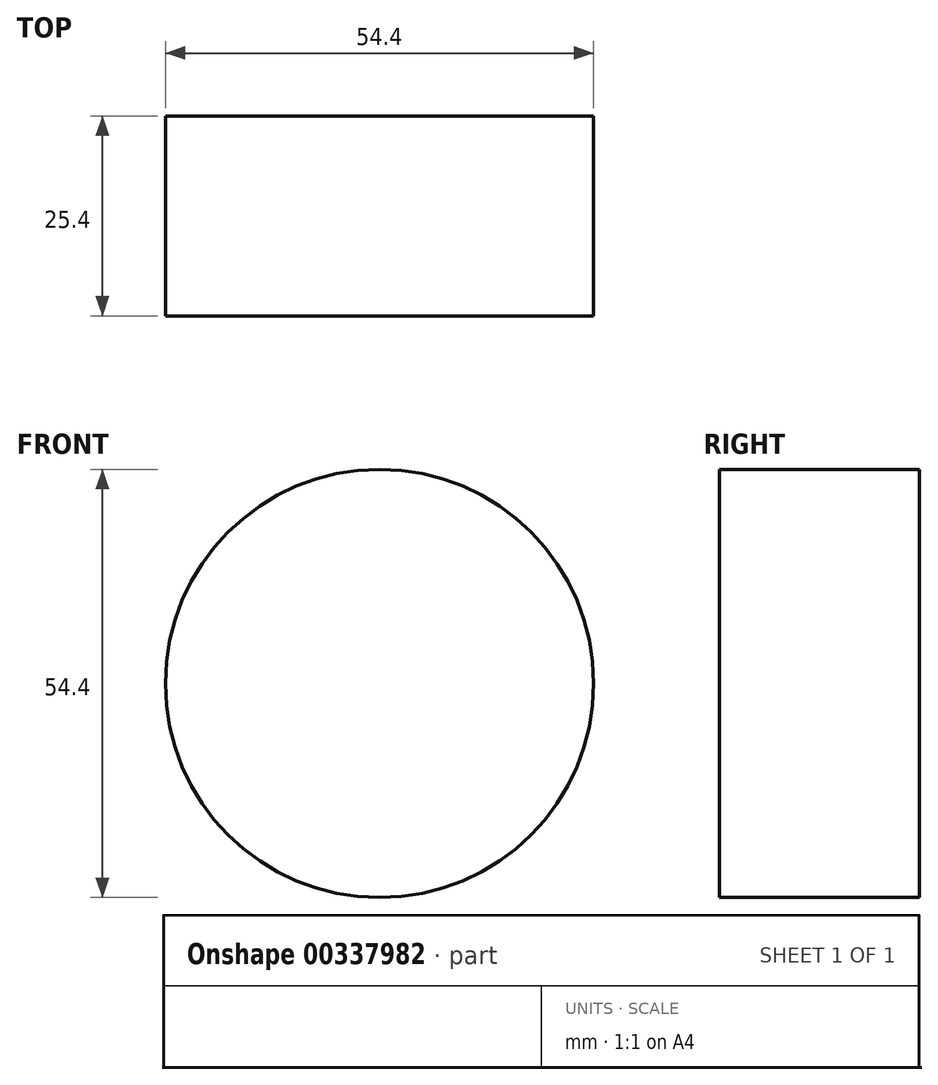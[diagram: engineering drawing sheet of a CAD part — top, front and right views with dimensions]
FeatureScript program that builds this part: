
annotation { "Feature Type Name" : "Feature", "Feature Type Description" : "" }
export const myFeature = defineFeature(function(context is Context, id is Id, definition is map)
    precondition{}
    {
        {
            var Q0;
            Q0=qCreatedBy(makeId("Front.planeOp"),FACE);
            var sketch = newSketch(context, id + "F0", { "sketchPlane" : qUnion([Q0])});
            skCircle(sketch, "E0", {"center": v(0, 0) * mm, "radius": 27.2 * mm});
            skSolve(sketch);
        }
        {
            var Q0;
            Q0=makeQuery(id+"F0.imprint","IMPRINT",FACE,{"disambiguationData":[TD([[makeQuery(id+"F0.imprint","IMPRINT",EDGE,{"derivedFrom":sQuery(id+"F0.wireOp",EDGE,"E0")}),1.0]])]});
            extrude(context, id + "F1", {"entities" : qUnion([Q0]), "depth" : 25.4 * mm});
        }
    });
